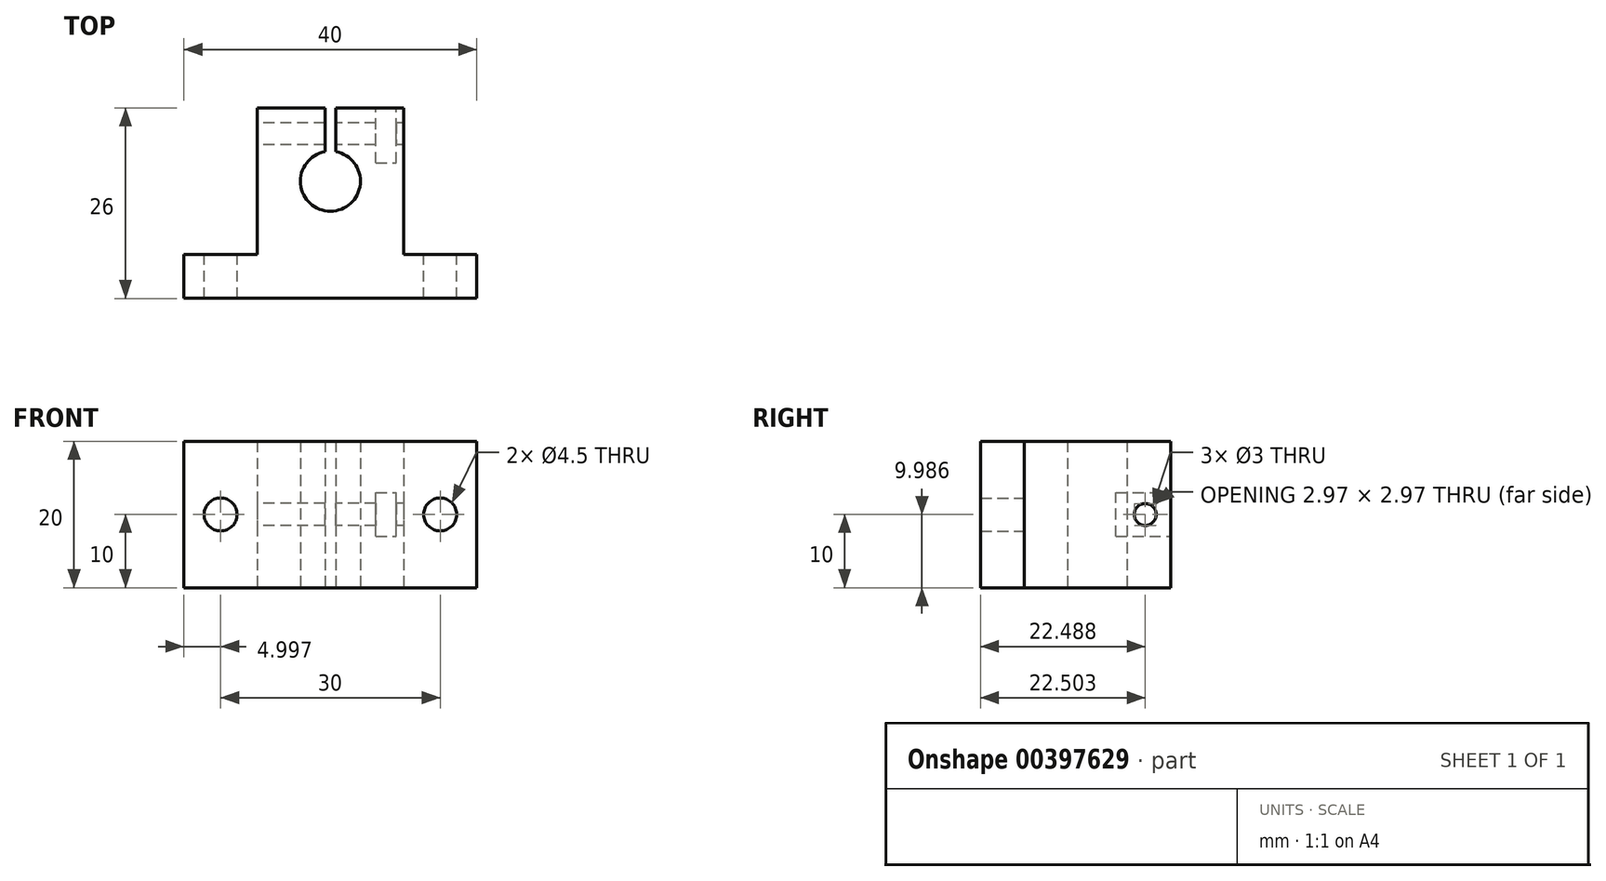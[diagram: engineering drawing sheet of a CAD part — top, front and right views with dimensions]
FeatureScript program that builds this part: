
annotation { "Feature Type Name" : "Feature", "Feature Type Description" : "" }
export const myFeature = defineFeature(function(context is Context, id is Id, definition is map)
    precondition{}
    {
        {
            var Q0;
            Q0=qCreatedBy(makeId("Top.planeOp"),FACE);
            var sketch = newSketch(context, id + "F0", { "sketchPlane" : qUnion([Q0])});
            skLineSegment(sketch, "E0.left", {"start": v(-48.33, -11.35) * mm, "end": v(-48.33, -5.35) * mm});
            skLineSegment(sketch, "E1.bottom", {"start": v(-38.33, -5.35) * mm, "end": v(-18.33, -5.35) * mm});
            skLineSegment(sketch, "E1.top", {"start": v(-38.33, 14.65) * mm, "end": v(-18.33, 14.65) * mm});
            skLineSegment(sketch, "E1.left", {"start": v(-38.33, -5.35) * mm, "end": v(-38.33, 14.65) * mm});
            skLineSegment(sketch, "E1.right", {"start": v(-18.33, -5.35) * mm, "end": v(-18.33, 14.65) * mm});
            skLineSegment(sketch, "E2", {"start": v(-8.33, -5.35) * mm, "end": v(-8.33, -11.35) * mm});
            skCircle(sketch, "E3", {"center": v(-28.33, 4.65) * mm, "radius": 4.1 * mm});
            skLineSegment(sketch, "E4.bottom", {"start": v(-29.08, 14.65) * mm, "end": v(-27.58, 14.65) * mm});
            skLineSegment(sketch, "E4.top", {"start": v(-29.08, 4.65) * mm, "end": v(-27.58, 4.65) * mm});
            skLineSegment(sketch, "E4.left", {"start": v(-29.08, 14.65) * mm, "end": v(-29.08, 4.65) * mm});
            skLineSegment(sketch, "E4.right", {"start": v(-27.58, 14.65) * mm, "end": v(-27.58, 4.65) * mm});
            skLineSegment(sketch, "E5", {"start": v(-48.33, -5.35) * mm, "end": v(-8.33, -5.35) * mm});
            skLineSegment(sketch, "E6", {"start": v(-8.33, -11.35) * mm, "end": v(-48.33, -11.35) * mm});
            skSolve(sketch);
        }
        {
            var Q0;
            {var subQ2=sQuery(id+"F0.wireOp",EDGE,"E1.left");Q0=makeQuery(id+"F0.imprint","IMPRINT",FACE,{"disambiguationData":[TD([[makeQuery(id+"F0.imprint","IMPRINT",EDGE,{"derivedFrom":subQ2}),-1.0]])]});}
            var Q1;
            {var subQ1=sQuery(id+"F0.wireOp",EDGE,"E0.left");Q1=makeQuery(id+"F0.imprint","IMPRINT",FACE,{"disambiguationData":[TD([[makeQuery(id+"F0.imprint","IMPRINT",EDGE,{"derivedFrom":subQ1}),-1.0]])]});}
            extrude(context, id + "F1", {"entities" : qUnion([Q0, Q1]), "depth" : 20 * mm});
        }
        {
            var Q0;
            Q0=makeQuery(id+"F1.opExtrude","SWEPT_FACE",FACE,{"disambiguationData":[OSD([sQuery(id+"F0.wireOp",EDGE,"E1.left")])]});
            var sketch = newSketch(context, id + "F2", { "sketchPlane" : qUnion([Q0])});
            skCircle(sketch, "E7", {"center": v(-11.15, 10) * mm, "radius": 1.5 * mm});
            skSolve(sketch);
        }
        {
            var Q0;
            Q0=qSketchRegion(id+"F2",true);
            extrude(context, id + "F3", {"entities" : qUnion([Q0]), "operationType" : NewBodyOperationType.REMOVE, "oppositeDirection" : true, "depth" : 20 * mm});
        }
        {
            var Q0;
            {var subQ0=sQuery(id+"F0.wireOp",EDGE,"E1.top");Q0=makeQuery(id+"F1.opExtrude","SWEPT_FACE",FACE,{"disambiguationData":[OSD([subQ0]),TDD([makeQuery(id+"F0.imprint","IMPRINT",EDGE,{"disambiguationData":[TD([[makeQuery(id+"F0.imprint","INTERSECT",VERTEX,{"derivedFrom":[subQ0,sQuery(id+"F0.wireOp",EDGE,"E1.left")]}),-1.0]])],"derivedFrom":subQ0})])]});}
            var sketch = newSketch(context, id + "F4", { "sketchPlane" : qUnion([Q0])});
            skLineSegment(sketch, "E8.bottom", {"start": v(22.13, 7) * mm, "end": v(19.33, 7) * mm});
            skLineSegment(sketch, "E8.top", {"start": v(22.13, 13) * mm, "end": v(19.33, 13) * mm});
            skLineSegment(sketch, "E8.left", {"start": v(22.13, 7) * mm, "end": v(22.13, 13) * mm});
            skLineSegment(sketch, "E8.right", {"start": v(19.33, 7) * mm, "end": v(19.33, 13) * mm});
            skSolve(sketch);
        }
        {
            var Q0;
            Q0=qSketchRegion(id+"F4",true);
            extrude(context, id + "F5", {"entities" : qUnion([Q0]), "operationType" : NewBodyOperationType.REMOVE, "oppositeDirection" : true, "depth" : 7.5 * mm});
        }
        {
            var Q0;
            {var subQ0=sQuery(id+"F0.wireOp",EDGE,"E5");Q0=makeQuery(id+"F1.opExtrude","SWEPT_FACE",FACE,{"disambiguationData":[OSD([subQ0]),TDD([makeQuery(id+"F0.imprint","IMPRINT",EDGE,{"disambiguationData":[TD([[makeQuery(id+"F0.imprint","INTERSECT",VERTEX,{"derivedFrom":[sQuery(id+"F0.wireOp",EDGE,"E0.left"),subQ0]}),-1.0]])],"derivedFrom":subQ0})])]});}
            var sketch = newSketch(context, id + "F6", { "sketchPlane" : qUnion([Q0])});
            skCircle(sketch, "E9", {"center": v(43.33, 10) * mm, "radius": 2.25 * mm});
            skLineSegment(sketch, "E10", {"start": v(28.33, 0) * mm, "end": v(28.33, 13.82) * mm});
            skCircle(sketch, "E11.MirrorC", {"center": v(13.33, 10) * mm, "radius": 2.25 * mm});
            skSolve(sketch);
        }
        {
            var Q0;
            Q0=qSketchRegion(id+"F6",true);
            extrude(context, id + "F7", {"entities" : qUnion([Q0]), "operationType" : NewBodyOperationType.REMOVE, "oppositeDirection" : true, "depth" : 6 * mm});
        }
    });
